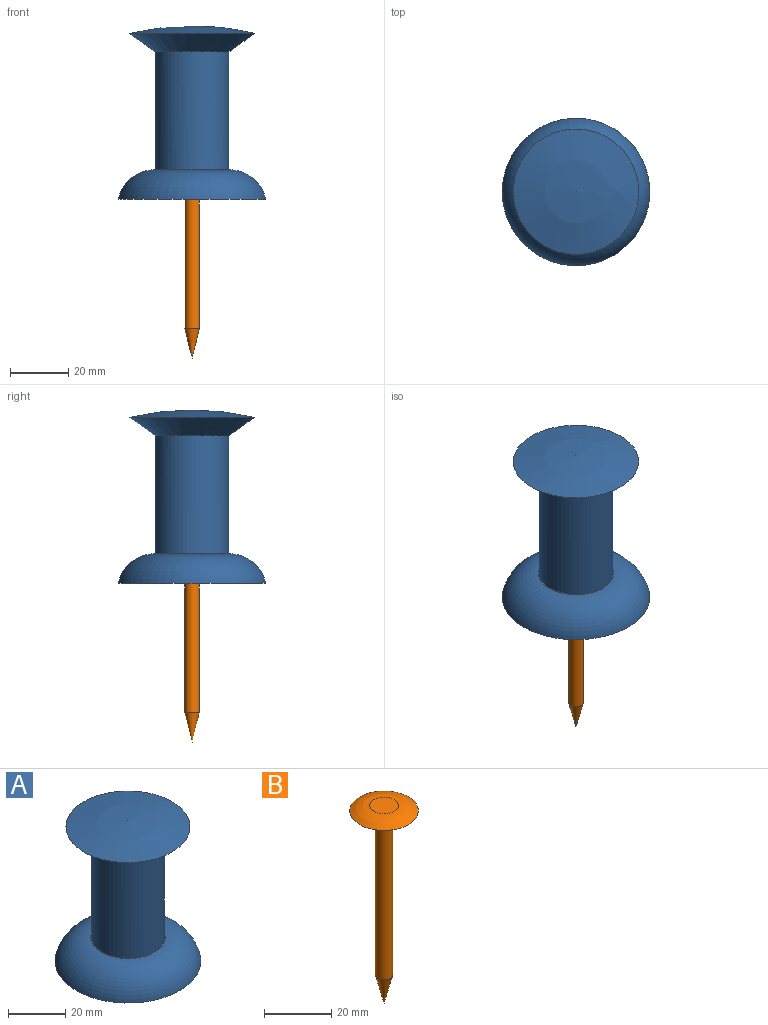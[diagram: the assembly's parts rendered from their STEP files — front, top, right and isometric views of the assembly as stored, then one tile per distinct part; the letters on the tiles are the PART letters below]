
ASSEMBLY  parts=2 mates=1
PART A: 6 faces, bbox 55.5x55.5x62.2 mm
  f0: plane 50.8x50.8mm, normal (0,0,-1), area 2026.8mm2, adj f4
  f1: cylinder r=12.7mm len=40.64mm, axis (0,0,-1), area 3242.9mm2, adj f2,f3
  f2: plane 25.91x25.91mm, normal (0,0,1), area 20.7mm2, adj f1,f4
  f3: cone r=12.7mm half-angle=54.5deg, axis (0,0,1), area 1176.9mm2, adj f1,f5
  f4: torus R=12.96mm, axis (0,0,1), area 2226.6mm2, adj f0,f2
  f5: sphere r=93.03mm, area 1484.7mm2, adj f3
PART B: 6 faces, bbox 20.3x20.3x71.8 mm
  f0: cylinder r=2.54mm len=54.61mm, axis (0,0,1), area 871.5mm2, adj f3,f4
  f1: plane 20.32x20.32mm, normal (0,0,-1), area 141.9mm2, adj f4,f5
  f2: plane 8.47x8.47mm, normal (0,0,1), area 56.4mm2, adj f5
  f3: cone r=2.54mm half-angle=14deg, axis (0,0,1), area 83.6mm2, adj f0
  f4: torus R=7.62mm, axis (0,0,1), area 219.9mm2, adj f0,f1
  f5: torus R=4.24mm, axis (0,0,-1), area 290mm2, adj f1,f2
PLACE A t=(-16.8,-7.47,6.2)mm
PLACE B t=(-16.8,-7.47,8.74)mm
MATE pin_slot A.f1 <-> B.f0  axis (0,0,-1) through (-16.8,-7.47,16.36)mm
